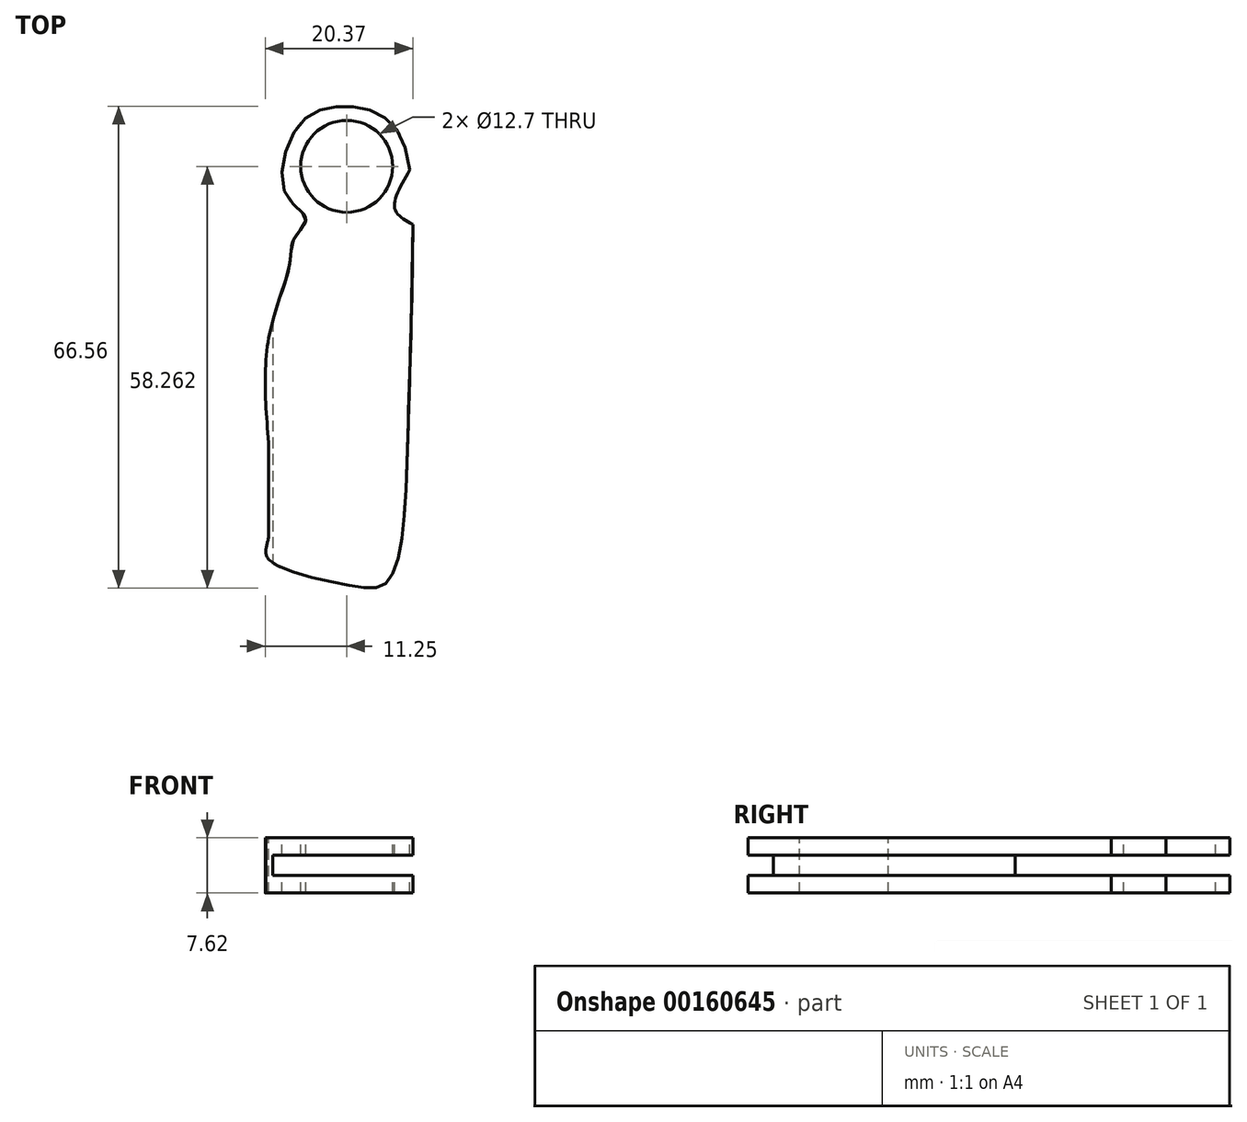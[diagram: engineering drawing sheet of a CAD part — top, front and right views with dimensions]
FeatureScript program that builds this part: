
annotation { "Feature Type Name" : "Feature", "Feature Type Description" : "" }
export const myFeature = defineFeature(function(context is Context, id is Id, definition is map)
    precondition{}
    {
        {
            var Q0;
            Q0=qCreatedBy(makeId("Top.planeOp"),FACE);
            var sketch = newSketch(context, id + "F0", { "sketchPlane" : qUnion([Q0])});
            skLineSegment(sketch, "E0.bottom", {"start": v(11.43, 36.34) * mm, "end": v(-11.43, 36.34) * mm});
            skLineSegment(sketch, "E0.top", {"start": v(11.43, -36.34) * mm, "end": v(-11.43, -36.34) * mm});
            skLineSegment(sketch, "E0.left", {"start": v(11.43, 36.34) * mm, "end": v(11.43, -36.34) * mm});
            skLineSegment(sketch, "E0.right", {"start": v(-11.43, 36.34) * mm, "end": v(-11.43, -36.34) * mm});
            skPoint(sketch, "E0.middle", {"position": v(0, 0) * mm});
            skSolve(sketch);
        }
        {
            var Q0;
            Q0=makeQuery(id+"F0.imprint","IMPRINT",FACE,{"disambiguationData":[TD([[makeQuery(id+"F0.imprint","IMPRINT",EDGE,{"derivedFrom":sQuery(id+"F0.wireOp",EDGE,"E0.bottom")}),1.0]])]});
            extrude(context, id + "F1", {"entities" : qUnion([Q0]), "depth" : 3.8 * mm});
        }
        {
            var Q0;
            Q0=makeQuery(id+"F1.opExtrude","CAP_FACE",FACE,{"disambiguationData":[OSD([sQuery(id+"F0.wireOp",EDGE,"E0.bottom"),sQuery(id+"F0.wireOp",EDGE,"E0.top"),sQuery(id+"F0.wireOp",EDGE,"E0.left"),sQuery(id+"F0.wireOp",EDGE,"E0.right")])],"isStart":true});
            extrude(context, id + "F2", {"entities" : qUnion([Q0]), "operationType" : NewBodyOperationType.ADD, "depth" : 3.8 * mm});
        }
        {
            var Q0;
            {var subQ0=sQuery(id+"F0.wireOp",EDGE,"E0.top");Q0=makeQuery(id+"F2.boolean.opBoolean","MERGE",FACE,{"derivedFrom":[makeQuery(id+"F1.opExtrude","SWEPT_FACE",FACE,{"disambiguationData":[OSD([subQ0])]}),makeQuery(id+"F2.opExtrude","SWEPT_FACE",FACE,{"disambiguationData":[OSD([subQ0])]})]});}
            var sketch = newSketch(context, id + "F3", { "sketchPlane" : qUnion([Q0])});
            skLineSegment(sketch, "E1.bottom", {"start": v(10.24, 1.4) * mm, "end": v(-10.24, 1.4) * mm});
            skLineSegment(sketch, "E1.top", {"start": v(10.24, -1.4) * mm, "end": v(-10.24, -1.4) * mm});
            skLineSegment(sketch, "E1.left", {"start": v(10.24, 1.4) * mm, "end": v(10.24, -1.4) * mm});
            skLineSegment(sketch, "E1.right", {"start": v(-10.24, 1.4) * mm, "end": v(-10.24, -1.4) * mm});
            skPoint(sketch, "E1.middle", {"position": v(0, 0) * mm});
            skLineSegment(sketch, "E2.bottom", {"start": v(11.43, 1.4) * mm, "end": v(9.04, 1.4) * mm});
            skLineSegment(sketch, "E2.top", {"start": v(11.43, -1.4) * mm, "end": v(9.04, -1.4) * mm});
            skLineSegment(sketch, "E2.left", {"start": v(11.43, 1.4) * mm, "end": v(11.43, -1.4) * mm});
            skLineSegment(sketch, "E2.right", {"start": v(9.04, 1.4) * mm, "end": v(9.04, -1.4) * mm});
            skPoint(sketch, "E2.middle", {"position": v(10.24, 0) * mm});
            skSolve(sketch);
        }
        {
            var Q0;
            Q0=makeQuery(id+"F3.imprint","IMPRINT",FACE,{"disambiguationData":[TD([[makeQuery(id+"F3.imprint","IMPRINT",EDGE,{"derivedFrom":sQuery(id+"F3.wireOp",EDGE,"E1.bottom")}),1.0]])]});
            var Q1;
            {var subQ0=sQuery(id+"F3.wireOp",EDGE,"E1.left");Q1=makeQuery(id+"F3.imprint","IMPRINT",FACE,{"disambiguationData":[TD([[makeQuery(id+"F3.imprint","IMPRINT",EDGE,{"derivedFrom":subQ0}),-1.0]])]});}
            var Q2;
            {var subQ0=sQuery(id+"F3.wireOp",EDGE,"E1.left");Q2=makeQuery(id+"F3.imprint","IMPRINT",FACE,{"disambiguationData":[TD([[makeQuery(id+"F3.imprint","IMPRINT",EDGE,{"derivedFrom":subQ0}),1.0]])]});}
            extrude(context, id + "F4", {"entities" : qUnion([Q0, Q1, Q2]), "operationType" : NewBodyOperationType.REMOVE, "oppositeDirection" : true, "depth" : 2540 * mm});
        }
        {
            var Q0;
            Q0=makeQuery(id+"F1.opExtrude","CAP_FACE",FACE,{"disambiguationData":[OSD([sQuery(id+"F0.wireOp",EDGE,"E0.bottom"),sQuery(id+"F0.wireOp",EDGE,"E0.top"),sQuery(id+"F0.wireOp",EDGE,"E0.left"),sQuery(id+"F0.wireOp",EDGE,"E0.right")])],"isStart":false});
            var sketch = newSketch(context, id + "F5", { "sketchPlane" : qUnion([Q0])});
            skLineSegment(sketch, "E3", {"start": v(0, 36.34) * mm, "end": v(0, 23.64) * mm});
            skCircle(sketch, "E4", {"center": v(0, 23.64) * mm, "radius": 6.35 * mm});
            skSolve(sketch);
        }
        {
            var Q0;
            Q0=makeQuery(id+"F5.imprint","IMPRINT",FACE,{"disambiguationData":[TD([[makeQuery(id+"F5.imprint","IMPRINT",EDGE,{"derivedFrom":sQuery(id+"F5.wireOp",EDGE,"E4")}),1.0]])]});
            extrude(context, id + "F6", {"entities" : qUnion([Q0]), "operationType" : NewBodyOperationType.REMOVE, "oppositeDirection" : true, "depth" : 25.4 * mm});
        }
        {
            var Q0;
            Q0=makeQuery(id+"F1.opExtrude","CAP_FACE",FACE,{"disambiguationData":[OSD([sQuery(id+"F0.wireOp",EDGE,"E0.bottom"),sQuery(id+"F0.wireOp",EDGE,"E0.top"),sQuery(id+"F0.wireOp",EDGE,"E0.left"),sQuery(id+"F0.wireOp",EDGE,"E0.right")])],"isStart":false});
            var sketch = newSketch(context, id + "F7", { "sketchPlane" : qUnion([Q0])});
            skLineSegment(sketch, "E5", {"start": v(-10.77, -36.34) * mm, "end": v(-10.77, 36.34) * mm});
            skPoint(sketch, "E6.0.internal.snap0", {"position": v(0, 36.34) * mm});
            skFitSpline(sketch, "E6", {"points": [v(0, 31.93) * mm, v(6.74, 28.95) * mm, v(9.1, 13.05) * mm, v(8.4, -15.04) * mm, v(5.74, -33.59) * mm, v(0, -34.2) * mm, v(-10.77, -30.66) * mm, v(-10.77, -27.46) * mm, v(-10.77, -15.2) * mm, v(-10.77, 0) * mm, v(-7.95, 9.85) * mm, v(-7.23, 13.71) * mm, v(-5.63, 16.42) * mm, v(-8.39, 19.73) * mm, v(-6.62, 29.33) * mm, v(0, 31.93) * mm]});
            skFitSpline(sketch, "E7", {"points": [v(8.72, 23.14) * mm, v(6.63, 17.85) * mm, v(9.12, 15.6) * mm], "startDerivative": vector(-6.23, -10.5) * mm, "endDerivative": vector(7.7, -4.3) * mm});
            skSolve(sketch);
        }
        {
            var Q0;
            {var subQ11=makeQuery(id+"F1.opExtrude","CAP_EDGE",EDGE,{"disambiguationData":[OSD([sQuery(id+"F0.wireOp",EDGE,"E0.left")])],"isStart":false});Q0=makeQuery(id+"F7.imprint","IMPRINT",FACE,{"disambiguationData":[TD([[makeQuery(id+"F7.imprint","IMPRINT",EDGE,{"derivedFrom":subQ11}),-1.0]])]});}
            var Q1;
            {var subQ10=makeQuery(id+"F1.opExtrude","CAP_EDGE",EDGE,{"disambiguationData":[OSD([sQuery(id+"F0.wireOp",EDGE,"E0.right")])],"isStart":false});Q1=makeQuery(id+"F7.imprint","IMPRINT",FACE,{"disambiguationData":[TD([[makeQuery(id+"F7.imprint","IMPRINT",EDGE,{"derivedFrom":subQ10}),1.0]])]});}
            var Q2;
            {var subQ0=sQuery(id+"F7.wireOp",EDGE,"E7");Q2=makeQuery(id+"F7.imprint","IMPRINT",FACE,{"disambiguationData":[TD([[makeQuery(id+"F7.imprint","IMPRINT",EDGE,{"derivedFrom":subQ0}),1.0]])]});}
            extrude(context, id + "F8", {"entities" : qUnion([Q0, Q1, Q2]), "operationType" : NewBodyOperationType.REMOVE, "oppositeDirection" : true, "depth" : 25.4 * mm});
        }
    });
